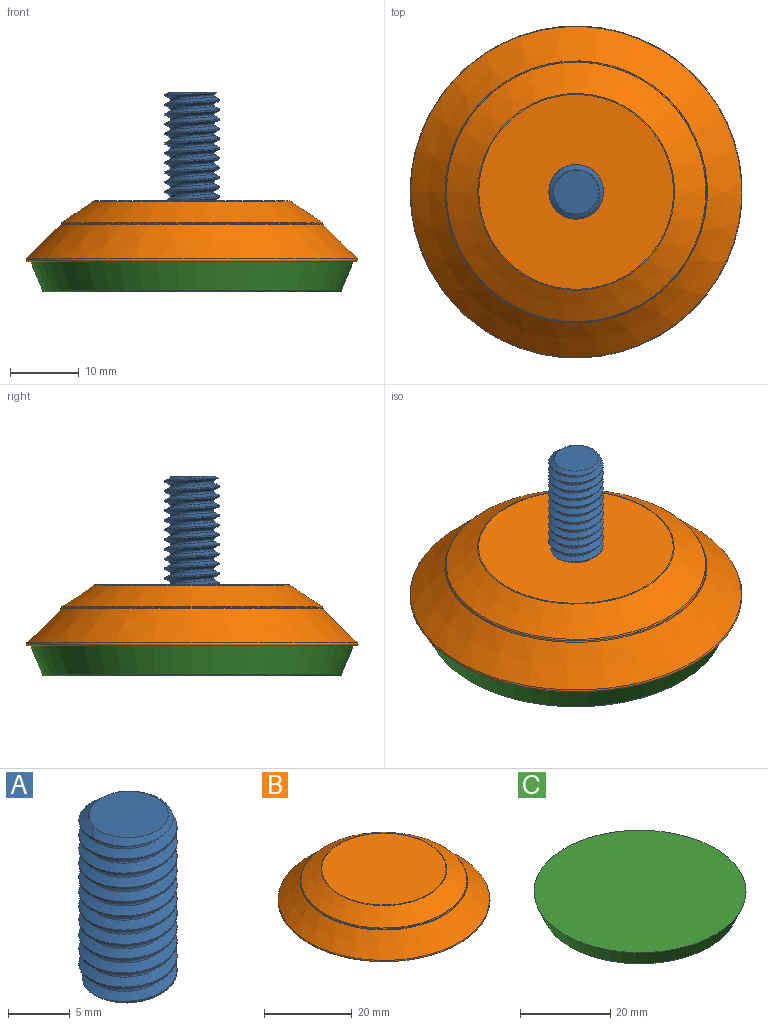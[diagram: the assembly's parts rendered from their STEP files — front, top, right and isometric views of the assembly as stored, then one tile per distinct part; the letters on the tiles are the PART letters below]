
ASSEMBLY  parts=3 mates=2
PART A: 7 faces, bbox 8.3x9.6x17.5 mm
  f0: cylinder r=3.97mm len=15.52mm, axis (0,0,-1), area 18.8mm2, adj f2,f4,f5,f6
  f1: plane 6.58x6.47mm, normal (0,0,1), area 32.9mm2, adj f3,f4,f5,f6
  f2: plane 7.51x7.46mm, normal (0,0,-1), area 39.3mm2, adj f0,f3,f4,f5
  f3: bspline ~16.82x7.4mm, area 88.2mm2, adj f1,f2,f4,f5
  f4: bspline ~17.14x9.17mm, area 221.7mm2, adj f0,f1,f2,f3,f6
  f5: bspline ~16.43x9.17mm, area 221.5mm2, adj f0,f1,f2,f3,f6
  f6: cone r=3.97mm half-angle=63.4deg, axis (0,0,-1), area 7.2mm2, adj f0,f1,f4,f5
PART B: 9 faces, bbox 52.5x52.5x8.9 mm
  f0: plane 47.95x47.95mm, normal (0,0,-1), area 1806mm2, adj f8
  f1: plane 28.42x28.42mm, normal (0,0,1), area 634.4mm2, adj f2
  f2: torus R=14.21mm, axis (0,0,-1), area 13.4mm2, adj f1,f3
  f3: cone r=14.35mm half-angle=56.3deg, axis (0,0,-1), area 576.3mm2, adj f2,f4
  f4: torus R=18.8mm, axis (0,0,-1), area 29.8mm2, adj f3,f5
  f5: cylinder r=19.05mm len=38.1mm, axis (0,0,-1), area 1.4mm2, adj f4,f6
  f6: torus R=19.3mm, axis (0,0,-1), area 24.1mm2, adj f5,f7
  f7: cone r=24.15mm half-angle=45.4deg, axis (0,0,-1), area 959.6mm2, adj f6,f8
  f8: torus R=23.98mm, axis (0,0,-1), area 91.1mm2, adj f0,f7
PART C: 4 faces, bbox 47.2x47.2x4.4 mm
  f0: plane 47.11x47.11mm, normal (0,0,1), area 1742.8mm2, adj f1
  f1: cone r=21.78mm half-angle=22.8deg, axis (0,0,1), area 650.9mm2, adj f0,f2
  f2: torus R=21.55mm, axis (0,0,-1), area 40.6mm2, adj f1,f3
  f3: plane 43.1x43.1mm, normal (0,0,-1), area 1458.7mm2, adj f2
PLACE A t=(0,0,-0.43)mm
PLACE B t=(0,0,-0.43)mm
PLACE C t=(0,0,-0.43)mm
MATE fastened C.f1 <-> B.f2  axis (0,0,1) through (0,0,-9.32)mm
MATE fastened A.f0 <-> B.f2  axis (0,0,1) through (0,0,-0.43)mm
